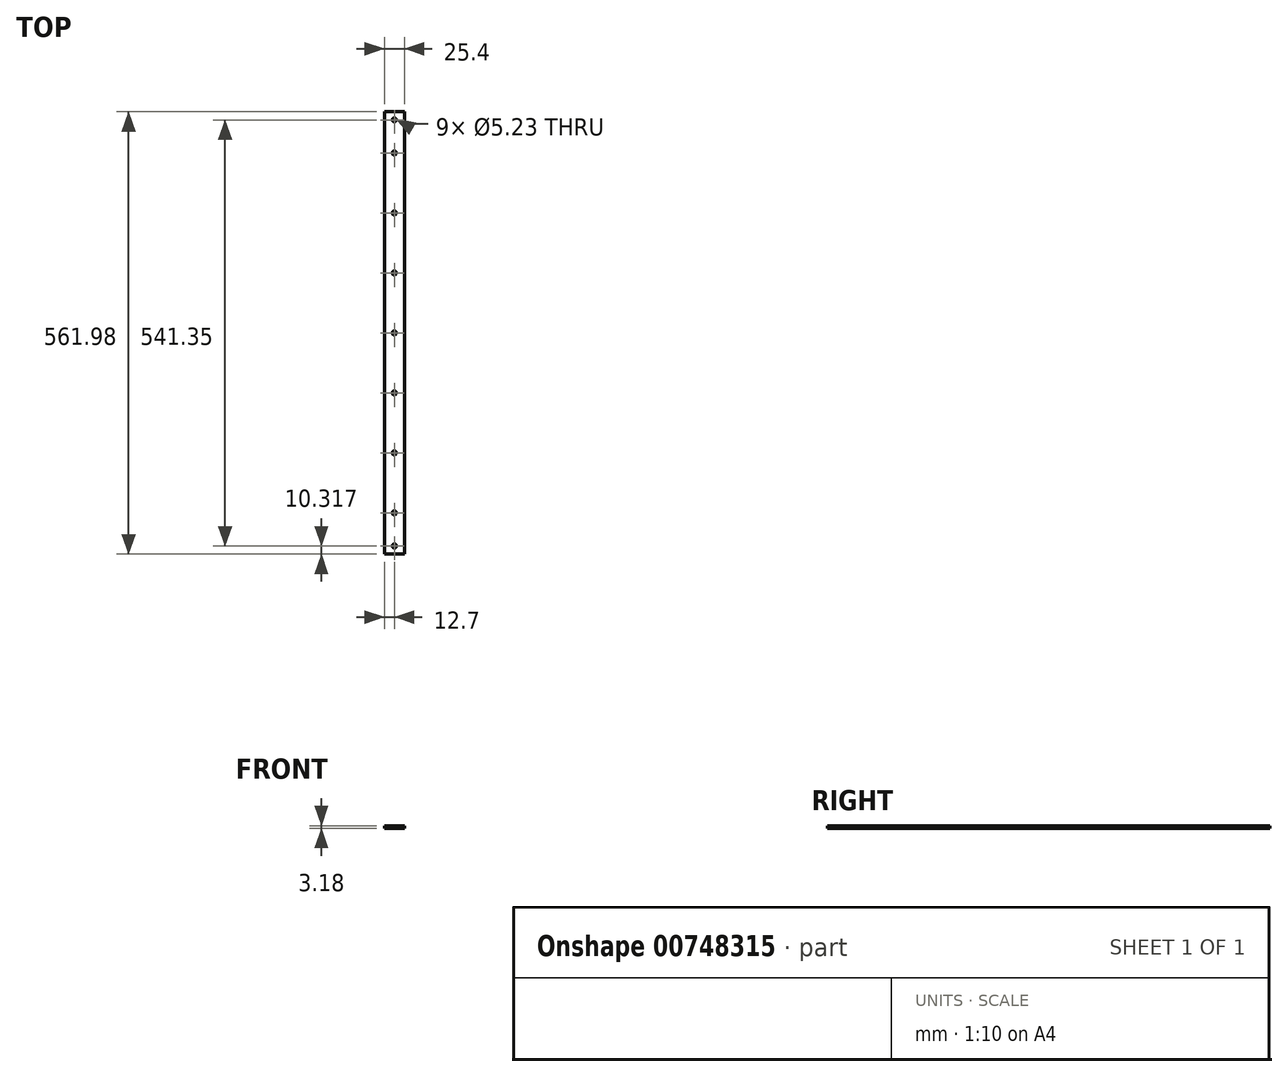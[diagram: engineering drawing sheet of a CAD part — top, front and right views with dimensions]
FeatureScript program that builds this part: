
annotation { "Feature Type Name" : "Feature", "Feature Type Description" : "" }
export const myFeature = defineFeature(function(context is Context, id is Id, definition is map)
    precondition{}
    {
        {
            var Q0;
            Q0=qCreatedBy(makeId("Front.planeOp"),FACE);
            var sketch = newSketch(context, id + "F0", { "sketchPlane" : qUnion([Q0])});
            skLineSegment(sketch, "E0.bottom", {"start": v(12.7, -1.59) * mm, "end": v(-12.7, -1.59) * mm});
            skLineSegment(sketch, "E0.top", {"start": v(12.7, 1.59) * mm, "end": v(-12.7, 1.59) * mm});
            skLineSegment(sketch, "E0.left", {"start": v(12.7, -1.59) * mm, "end": v(12.7, 1.59) * mm});
            skLineSegment(sketch, "E0.right", {"start": v(-12.7, -1.59) * mm, "end": v(-12.7, 1.59) * mm});
            skPoint(sketch, "E0.middle", {"position": v(0, 0) * mm});
            skSolve(sketch);
        }
        {
            var Q0;
            Q0=qSketchRegion(id+"F0",true);
            extrude(context, id + "F1", {"entities" : qUnion([Q0]), "depth" : 561.98 * mm, "offsetDistance" : 25.4 * mm});
        }
        {
            var Q0;
            Q0=makeQuery(id+"F1.opExtrude","SWEPT_FACE",FACE,{"disambiguationData":[OSD([sQuery(id+"F0.wireOp",EDGE,"E0.top")])]});
            var sketch = newSketch(context, id + "F2", { "sketchPlane" : qUnion([Q0])});
            skLineSegment(sketch, "E1", {"start": v(0, -561.98) * mm, "end": v(0, 0) * mm, "construction": true});
            skLineSegment(sketch, "E2", {"start": v(-12.7, -551.66) * mm, "end": v(12.7, -551.66) * mm, "construction": true});
            skLineSegment(sketch, "E3", {"start": v(-12.7, -10.31) * mm, "end": v(12.7, -10.31) * mm, "construction": true});
            skLineSegment(sketch, "E4", {"start": v(-12.7, -280.99) * mm, "end": v(12.7, -280.99) * mm, "construction": true});
            skLineSegment(sketch, "E5.0", {"start": v(-12.7, -357.19) * mm, "end": v(12.7, -357.19) * mm, "construction": true});
            skLineSegment(sketch, "E6.0", {"start": v(-12.7, -433.39) * mm, "end": v(12.7, -433.39) * mm, "construction": true});
            skLineSegment(sketch, "E7.0", {"start": v(-12.7, -509.59) * mm, "end": v(12.7, -509.59) * mm, "construction": true});
            skLineSegment(sketch, "E8.0", {"start": v(-12.7, -204.79) * mm, "end": v(12.7, -204.79) * mm, "construction": true});
            skLineSegment(sketch, "E9.0", {"start": v(-12.7, -128.59) * mm, "end": v(12.7, -128.59) * mm, "construction": true});
            skLineSegment(sketch, "E10.0", {"start": v(-12.7, -52.39) * mm, "end": v(12.7, -52.39) * mm, "construction": true});
            skCircle(sketch, "E11", {"center": v(0, -551.66) * mm, "radius": 2.62 * mm});
            skCircle(sketch, "E12", {"center": v(0, -509.59) * mm, "radius": 2.62 * mm});
            skCircle(sketch, "E13", {"center": v(0, -433.39) * mm, "radius": 2.62 * mm});
            skCircle(sketch, "E14", {"center": v(0, -357.19) * mm, "radius": 2.62 * mm});
            skCircle(sketch, "E15", {"center": v(0, -280.99) * mm, "radius": 2.62 * mm});
            skCircle(sketch, "E16", {"center": v(0, -204.79) * mm, "radius": 2.62 * mm});
            skCircle(sketch, "E17", {"center": v(0, -128.59) * mm, "radius": 2.62 * mm});
            skCircle(sketch, "E18", {"center": v(0, -52.39) * mm, "radius": 2.62 * mm});
            skCircle(sketch, "E19", {"center": v(0, -10.31) * mm, "radius": 2.62 * mm});
            skSolve(sketch);
        }
        {
            var Q0;
            Q0=qSketchRegion(id+"F2",true);
            extrude(context, id + "F3", {"entities" : qUnion([Q0]), "operationType" : NewBodyOperationType.REMOVE, "endBound" : BoundingType.THROUGH_ALL, "oppositeDirection" : true, "depth" : 25.4 * mm, "offsetDistance" : 25.4 * mm});
        }
    });
